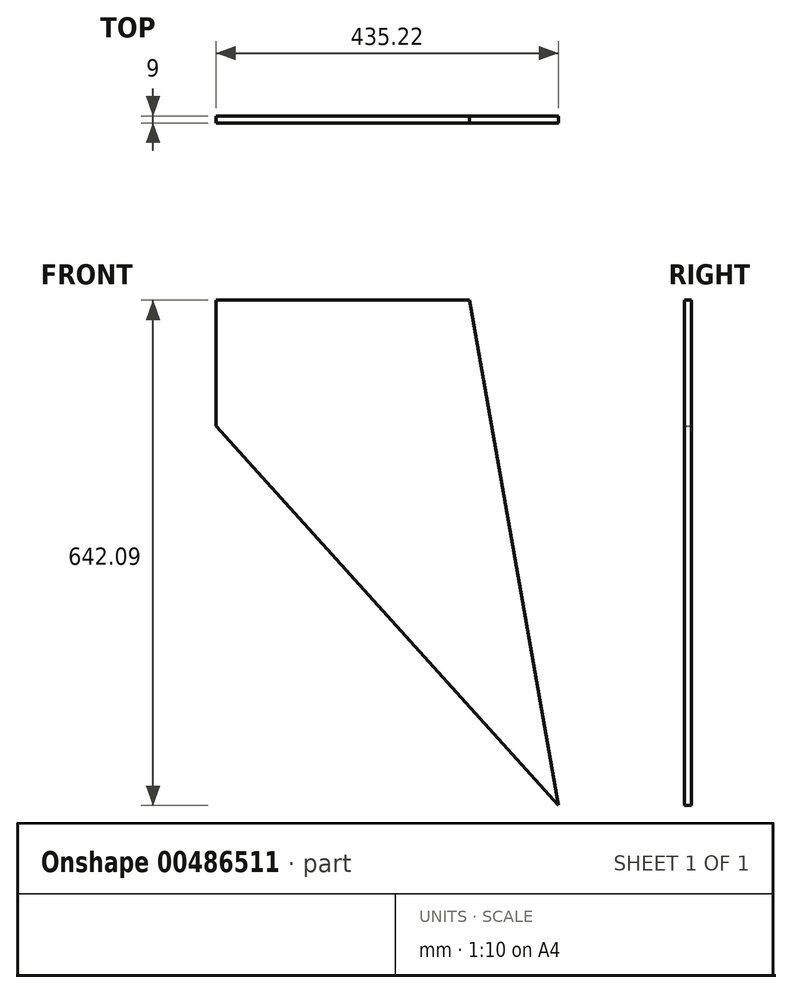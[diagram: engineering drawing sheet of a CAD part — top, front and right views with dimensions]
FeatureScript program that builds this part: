
annotation { "Feature Type Name" : "Feature", "Feature Type Description" : "" }
export const myFeature = defineFeature(function(context is Context, id is Id, definition is map)
    precondition{}
    {
        {
            var Q0;
            Q0=qCreatedBy(makeId("Front.planeOp"),FACE);
            var sketch = newSketch(context, id + "F0", { "sketchPlane" : qUnion([Q0])});
            skLineSegment(sketch, "E0", {"start": v(324.78, 0.15) * mm, "end": v(2.78, 0.15) * mm});
            skLineSegment(sketch, "E1", {"start": v(2.78, 0.15) * mm, "end": v(2.78, -159.85) * mm});
            skLineSegment(sketch, "E2", {"start": v(2.78, -159.85) * mm, "end": v(438, -641.94) * mm});
            skLineSegment(sketch, "E3", {"start": v(438, -641.94) * mm, "end": v(324.78, 0.15) * mm});
            skSolve(sketch);
        }
        {
            var Q0;
            Q0=makeQuery(id+"F0.imprint","IMPRINT",FACE,{"disambiguationData":[TD([[makeQuery(id+"F0.imprint","IMPRINT",EDGE,{"derivedFrom":sQuery(id+"F0.wireOp",EDGE,"E0")}),1.0]])]});
            extrude(context, id + "F1", {"entities" : qUnion([Q0]), "depth" : 9 * mm, "offsetDistance" : 25 * mm});
        }
    });
